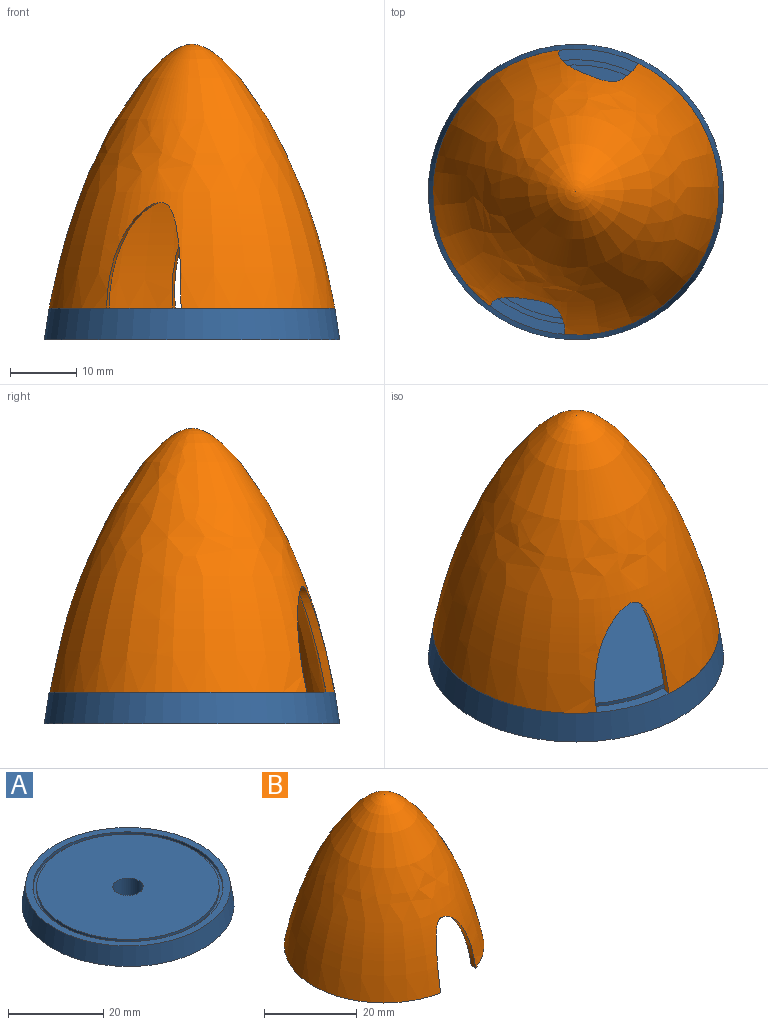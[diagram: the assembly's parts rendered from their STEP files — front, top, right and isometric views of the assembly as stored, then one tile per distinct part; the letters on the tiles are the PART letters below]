
ASSEMBLY  parts=2 mates=1
PART A: 12 faces, bbox 44.5x44.5x4.8 mm
  f0: plane 40.32x40.32mm, normal (0,0,-1), area 1150.1mm2, adj f1,f11
  f1: cone r=20.16mm half-angle=8.6deg, axis (0,0,-1), area 411.5mm2, adj f0,f2
  f2: plane 44.45x44.45mm, normal (0,0,-1), area 213.8mm2, adj f1,f3
  f3: cone r=21.51mm half-angle=8.6deg, axis (0,0,-1), area 661.7mm2, adj f2,f4
  f4: plane 43.02x43.02mm, normal (0,0,1), area 206.6mm2, adj f3,f5
  f5: cylinder r=19.92mm len=39.84mm, axis (0,0,-1), area 99.4mm2, adj f4,f6
  f6: plane 39.84x39.84mm, normal (0,0,1), area 97.4mm2, adj f5,f7
  f7: cylinder r=19.13mm len=38.25mm, axis (0,0,-1), area 95.4mm2, adj f6,f8
  f8: plane 38.25x38.25mm, normal (0,0,1), area 1117.7mm2, adj f7,f9
  f9: cylinder r=3.17mm len=6.35mm, axis (0,0,-1), area 95mm2, adj f8,f10
  f10: plane 12.7x12.7mm, normal (0,0,-1), area 95mm2, adj f9,f11
  f11: cylinder r=6.35mm len=12.7mm, axis (0,0,-1), area 126.7mm2, adj f0,f10
PART B: 6 faces, bbox 43x43x39.7 mm
  f0: plane 42.28x17.54mm, normal (0,0,-1), area 74.2mm2, adj f2,f3,f4,f5
  f1: plane 39.98x13.57mm, normal (0,0,-1), area 63.5mm2, adj f2,f3,f4,f5
  f2: revolved ~43.02x43.02mm, area 3651.8mm2, adj f0,f1,f4,f5
  f3: revolved ~40.44x40.44mm, area 3236.6mm2, adj f0,f1,f4,f5
  f4: extruded ~15.88x11.94mm, area 49.6mm2, adj f0,f1,f2,f3
  f5: extruded ~15.88x11.94mm, area 49.6mm2, adj f0,f1,f2,f3
PLACE A rot(axis=(0,0,1),165deg) t=(1.85,-0.35,-4.5)mm
PLACE B rot(axis=(0,0,1),165deg) t=(1.85,-0.35,-4.5)mm
MATE fastened B.f0 <-> A.f1  axis (0,0,1) through (1.85,-0.35,0.26)mm
